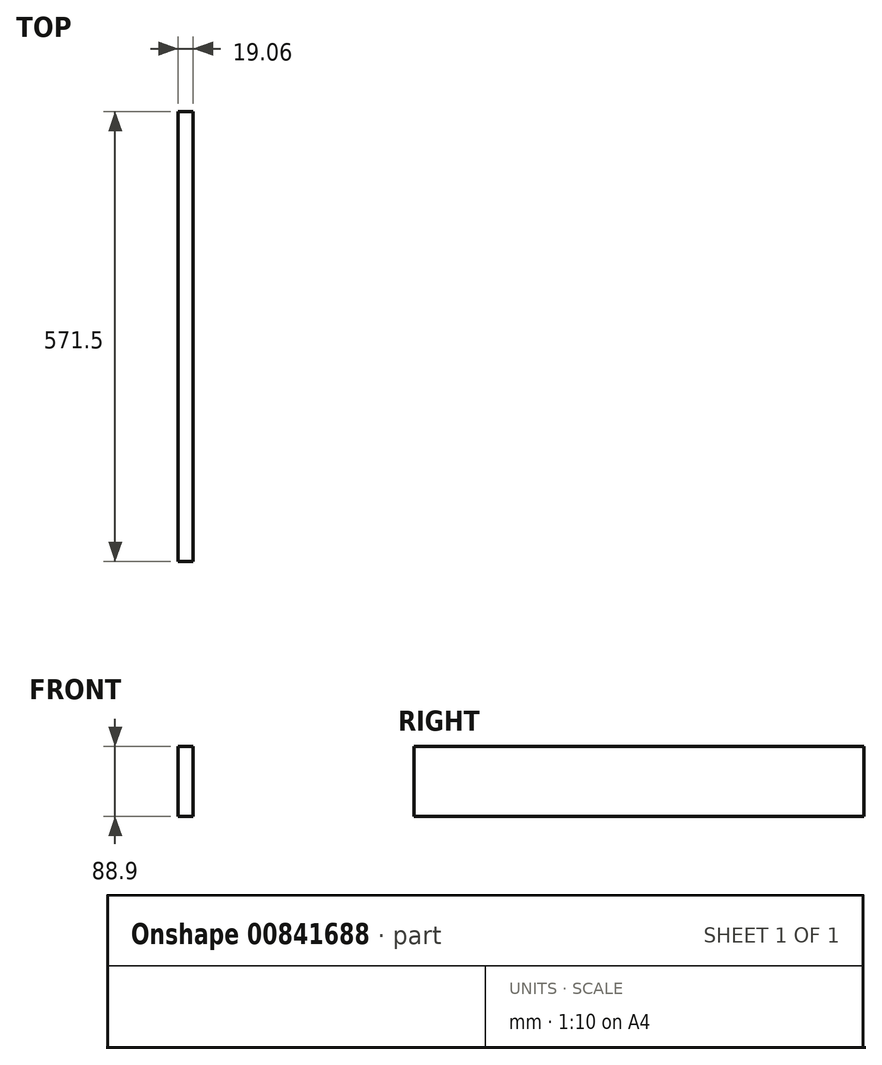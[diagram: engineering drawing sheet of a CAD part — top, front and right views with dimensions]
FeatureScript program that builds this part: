
annotation { "Feature Type Name" : "Feature", "Feature Type Description" : "" }
export const myFeature = defineFeature(function(context is Context, id is Id, definition is map)
    precondition{}
    {
        {
            var Q0;
            Q0=qCreatedBy(makeId("Front.planeOp"),FACE);
            var sketch = newSketch(context, id + "F0", { "sketchPlane" : qUnion([Q0])});
            skLineSegment(sketch, "E0.bottom", {"start": v(9.52, -44.45) * mm, "end": v(-9.53, -44.45) * mm});
            skLineSegment(sketch, "E0.top", {"start": v(9.53, 44.45) * mm, "end": v(-9.52, 44.45) * mm});
            skLineSegment(sketch, "E0.left", {"start": v(9.52, -44.45) * mm, "end": v(9.53, 44.45) * mm});
            skLineSegment(sketch, "E0.right", {"start": v(-9.53, -44.45) * mm, "end": v(-9.52, 44.45) * mm});
            skPoint(sketch, "E0.middle", {"position": v(0, 0) * mm});
            skSolve(sketch);
        }
        {
            var Q0;
            Q0 = qSketchRegion(id + "F0", true);
            extrude(context, id + "F1", {"entities" : qUnion([Q0]), "depth" : 571.5 * mm, "offsetDistance" : 25.4 * mm});
        }
    });
